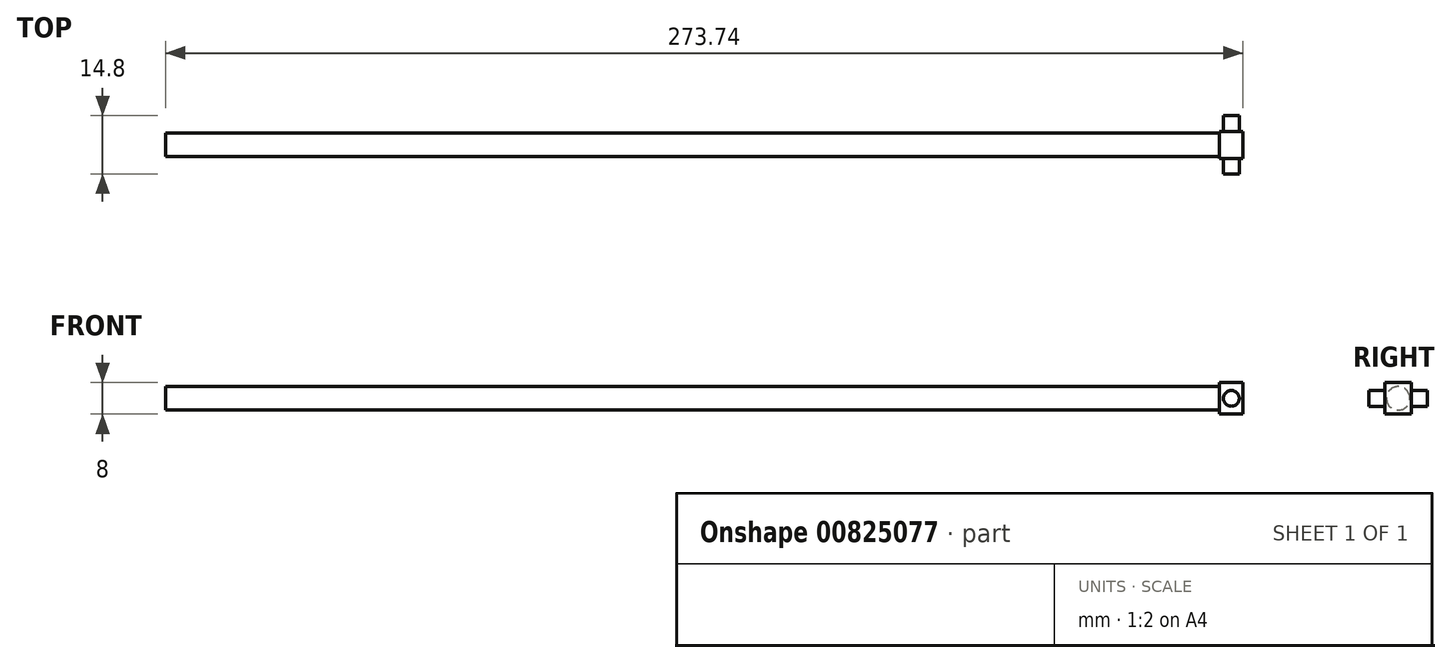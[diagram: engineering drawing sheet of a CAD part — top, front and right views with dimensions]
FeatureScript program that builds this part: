
annotation { "Feature Type Name" : "Feature", "Feature Type Description" : "" }
export const myFeature = defineFeature(function(context is Context, id is Id, definition is map)
    precondition{}
    {
        {
            var Q0;
            Q0=qCreatedBy(makeId("Front.planeOp"),FACE);
            var sketch = newSketch(context, id + "F0", { "sketchPlane" : qUnion([Q0])});
            skLineSegment(sketch, "E0.bottom", {"start": v(-3, 4) * mm, "end": v(3, 4) * mm});
            skLineSegment(sketch, "E0.top", {"start": v(-3, -4) * mm, "end": v(3, -4) * mm});
            skLineSegment(sketch, "E0.left", {"start": v(-3, 4) * mm, "end": v(-3, -4) * mm});
            skLineSegment(sketch, "E0.right", {"start": v(3, 4) * mm, "end": v(3, -4) * mm});
            skPoint(sketch, "E0.middle", {"position": v(0, 0) * mm});
            skSolve(sketch);
        }
        {
            var Q0;
            Q0=makeQuery(id+"F0.imprint","IMPRINT",FACE,{"disambiguationData":[TD([[makeQuery(id+"F0.imprint","IMPRINT",EDGE,{"derivedFrom":sQuery(id+"F0.wireOp",EDGE,"E0.bottom")}),-1.0]])]});
            extrude(context, id + "F1", {"entities" : qUnion([Q0]), "endBound" : BoundingType.SYMMETRIC, "depth" : (6.8 + 8) * mm, "offsetDistance" : 25 * mm});
        }
        {
            var Q0;
            Q0=makeQuery(id+"F1.opExtrude","CAP_FACE",FACE,{"disambiguationData":[OSD([sQuery(id+"F0.wireOp",EDGE,"E0.bottom"),sQuery(id+"F0.wireOp",EDGE,"E0.top"),sQuery(id+"F0.wireOp",EDGE,"E0.left"),sQuery(id+"F0.wireOp",EDGE,"E0.right")])],"isStart":false});
            var sketch = newSketch(context, id + "F2", { "sketchPlane" : qUnion([Q0])});
            skCircle(sketch, "E1", {"center": v(0, 0) * mm, "radius": 2 * mm});
            skSolve(sketch);
        }
        {
            var Q0;
            Q0=makeQuery(id+"F2.imprint","IMPRINT",FACE,{"disambiguationData":[TD([[makeQuery(id+"F2.imprint","IMPRINT",EDGE,{"derivedFrom":sQuery(id+"F2.wireOp",EDGE,"E1")}),-1.0]])]});
            extrude(context, id + "F3", {"entities" : qUnion([Q0]), "operationType" : NewBodyOperationType.REMOVE, "oppositeDirection" : true, "depth" : 4 * mm, "offsetDistance" : 25 * mm});
        }
        {
            var Q0;
            Q0=makeQuery(id+"F1.opExtrude","CAP_FACE",FACE,{"disambiguationData":[OSD([sQuery(id+"F0.wireOp",EDGE,"E0.bottom"),sQuery(id+"F0.wireOp",EDGE,"E0.top"),sQuery(id+"F0.wireOp",EDGE,"E0.left"),sQuery(id+"F0.wireOp",EDGE,"E0.right")])],"isStart":true});
            var sketch = newSketch(context, id + "F4", { "sketchPlane" : qUnion([Q0])});
            skCircle(sketch, "E2", {"center": v(0, 0) * mm, "radius": 2 * mm});
            skSolve(sketch);
        }
        {
            var Q0;
            Q0=makeQuery(id+"F4.imprint","IMPRINT",FACE,{"disambiguationData":[TD([[makeQuery(id+"F4.imprint","IMPRINT",EDGE,{"derivedFrom":sQuery(id+"F4.wireOp",EDGE,"E2")}),-1.0]])]});
            extrude(context, id + "F5", {"entities" : qUnion([Q0]), "operationType" : NewBodyOperationType.REMOVE, "oppositeDirection" : true, "depth" : 4 * mm, "offsetDistance" : 25 * mm});
        }
        {
            var Q0;
            Q0=makeQuery(id+"F1.opExtrude","SWEPT_FACE",FACE,{"disambiguationData":[OSD([sQuery(id+"F0.wireOp",EDGE,"E0.left")])]});
            var sketch = newSketch(context, id + "F6", { "sketchPlane" : qUnion([Q0])});
            skCircle(sketch, "E3", {"center": v(0, 0) * mm, "radius": 3 * mm});
            skSolve(sketch);
        }
        {
            var Q0;
            Q0=makeQuery(id+"F6.imprint","IMPRINT",FACE,{"disambiguationData":[TD([[makeQuery(id+"F6.imprint","IMPRINT",EDGE,{"derivedFrom":sQuery(id+"F6.wireOp",EDGE,"E3")}),1.0]])]});
            extrude(context, id + "F7", {"entities" : qUnion([Q0]), "operationType" : NewBodyOperationType.ADD, "depth" : (170.74 - 3) * mm, "offsetDistance" : 25 * mm});
        }
        {
            var Q0;
            Q0=makeQuery(id+"F7.opExtrude","CAP_FACE",FACE,{"disambiguationData":[OSD([sQuery(id+"F6.wireOp",EDGE,"E3")])],"isStart":false});
            var sketch = newSketch(context, id + "F8", { "sketchPlane" : qUnion([Q0])});
            skCircle(sketch, "E4", {"center": v(0, 0) * mm, "radius": 3 * mm});
            skSolve(sketch);
        }
        {
            var Q0;
            Q0=makeQuery(id+"F8.imprint","IMPRINT",FACE,{"disambiguationData":[TD([[makeQuery(id+"F8.imprint","IMPRINT",EDGE,{"derivedFrom":sQuery(id+"F8.wireOp",EDGE,"E4")}),1.0]])]});
            extrude(context, id + "F9", {"entities" : qUnion([Q0]), "operationType" : NewBodyOperationType.ADD, "depth" : 100 * mm, "offsetDistance" : 25 * mm});
        }
    });
